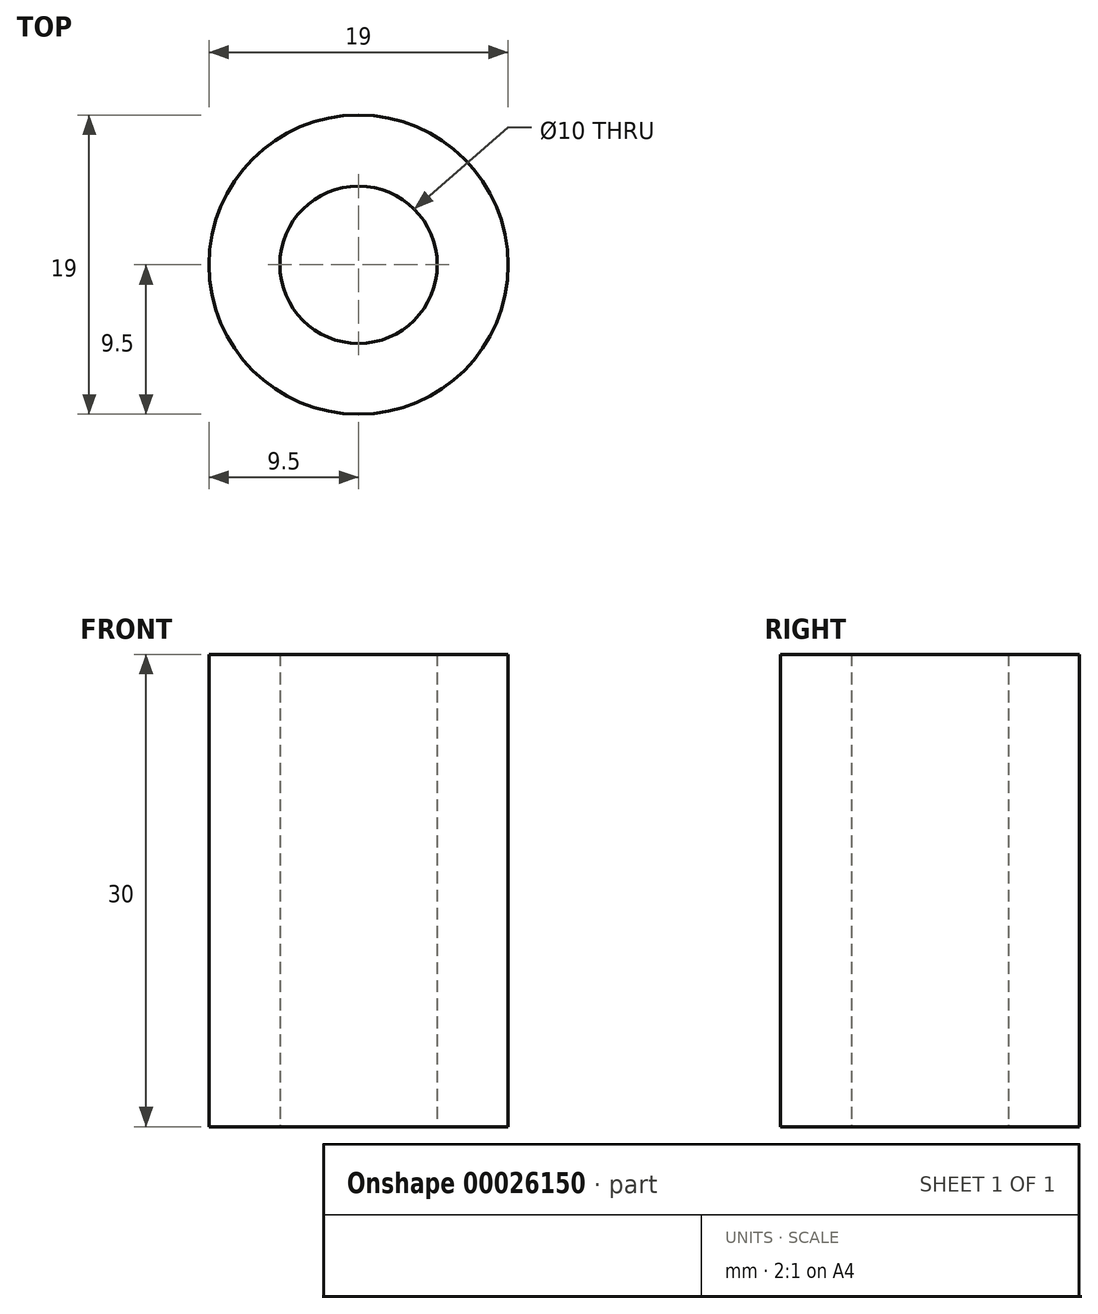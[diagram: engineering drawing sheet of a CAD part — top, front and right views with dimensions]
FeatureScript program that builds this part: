
annotation { "Feature Type Name" : "Feature", "Feature Type Description" : "" }
export const myFeature = defineFeature(function(context is Context, id is Id, definition is map)
    precondition{}
    {
        {
            var Q0;
            Q0=qCreatedBy(makeId("Top.planeOp"),FACE);
            var sketch = newSketch(context, id + "F0", { "sketchPlane" : qUnion([Q0])});
            skCircle(sketch, "E0", {"center": v(0, 0) * mm, "radius": 9.5 * mm});
            skCircle(sketch, "E1", {"center": v(0, 0) * mm, "radius": 5 * mm});
            skSolve(sketch);
        }
        {
            var Q0;
            Q0=makeQuery(id+"F0.imprint","IMPRINT",FACE,{"disambiguationData":[TD([[makeQuery(id+"F0.imprint","IMPRINT",EDGE,{"derivedFrom":sQuery(id+"F0.wireOp",EDGE,"E0")}),1.0]])]});
            extrude(context, id + "F1", {"entities" : qUnion([Q0]), "depth" : 30 * mm});
        }
    });
